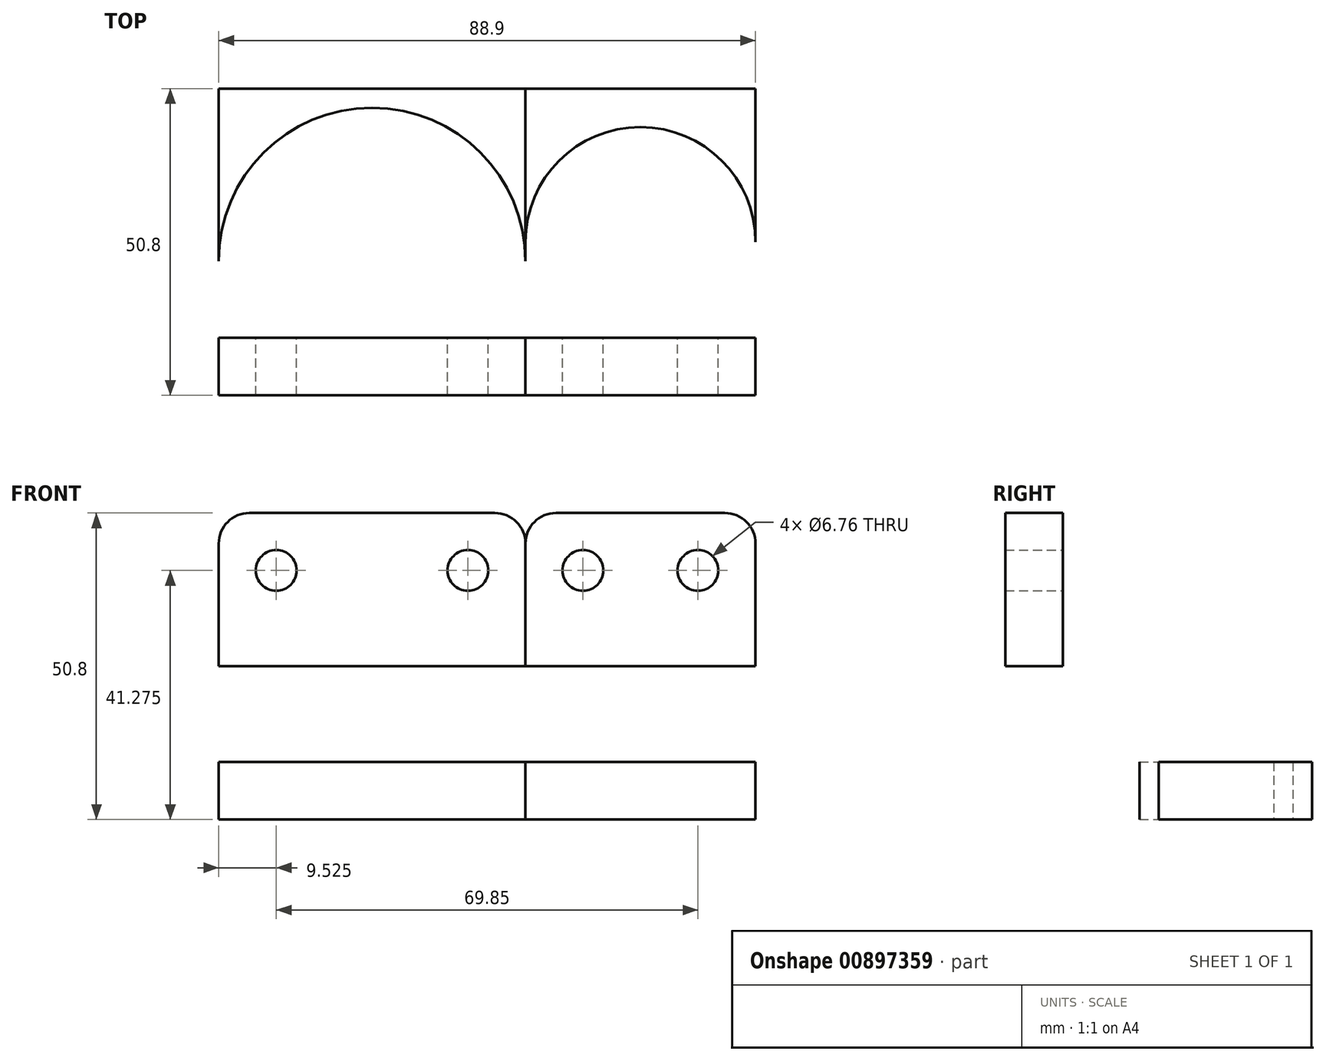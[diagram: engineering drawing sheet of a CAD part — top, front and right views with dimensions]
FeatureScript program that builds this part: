
annotation { "Feature Type Name" : "Feature", "Feature Type Description" : "" }
export const myFeature = defineFeature(function(context is Context, id is Id, definition is map)
    precondition{}
    {
        {
            var Q0;
            Q0=qCreatedBy(makeId("Right.planeOp"),FACE);
            var sketch = newSketch(context, id + "F0", { "sketchPlane" : qUnion([Q0])});
            skLineSegment(sketch, "E0", {"start": v(0, 50.8) * mm, "end": v(0, 0) * mm});
            skLineSegment(sketch, "E1", {"start": v(0, 0) * mm, "end": v(50.8, 0) * mm});
            skLineSegment(sketch, "E2.0", {"start": v(9.53, 9.53) * mm, "end": v(50.8, 9.53) * mm});
            skLineSegment(sketch, "E2.1", {"start": v(9.53, 50.8) * mm, "end": v(9.53, 9.53) * mm});
            skLineSegment(sketch, "E3", {"start": v(0, 50.8) * mm, "end": v(9.53, 50.8) * mm});
            skLineSegment(sketch, "E4", {"start": v(50.8, 9.53) * mm, "end": v(50.8, 0) * mm});
            skSolve(sketch);
        }
        {
            var Q0;
            Q0=makeQuery(id+"F0.imprint","IMPRINT",FACE,{"disambiguationData":[TD([[makeQuery(id+"F0.imprint","IMPRINT",EDGE,{"derivedFrom":sQuery(id+"F0.wireOp",EDGE,"E0")}),1.0]])]});
            extrude(context, id + "F1", {"entities" : qUnion([Q0]), "depth" : 38.1 * mm, "offsetDistance" : 25.4 * mm});
        }
        {
            var Q0;
            Q0 = qSketchRegion(id + "F0", true);
            extrude(context, id + "F2", {"entities" : qUnion([Q0]), "oppositeDirection" : true, "depth" : 50.8 * mm, "offsetDistance" : 25.4 * mm});
        }
        {
            var Q0;
            Q0=makeQuery(id+"F1.opExtrude","SWEPT_FACE",FACE,{"disambiguationData":[OSD([sQuery(id+"F0.wireOp",EDGE,"E1")])]});
            var sketch = newSketch(context, id + "F3", { "sketchPlane" : qUnion([Q0])});
            skCircle(sketch, "E5", {"center": v(19.05, -22.23) * mm, "radius": 6.35 * mm});
            skPoint(sketch, "E6", {"position": v(19.05, -25.4) * mm});
            skArc(sketch, "E7", {"start": v(38.1, -25.4) * mm, "mid": v(19.05, -44.45) * mm, "end": v(0, -25.4) * mm});
            skPoint(sketch, "E8", {"position": v(19.05, -44.45) * mm});
            skLineSegment(sketch, "E9", {"start": v(38.1, -9.52) * mm, "end": v(0, -9.53) * mm, "construction": true});
            skSolve(sketch);
        }
        {
            var Q0;
            Q0=makeQuery(id+"F2.opExtrude","SWEPT_FACE",FACE,{"disambiguationData":[OSD([sQuery(id+"F0.wireOp",EDGE,"E1")])]});
            var sketch = newSketch(context, id + "F4", { "sketchPlane" : qUnion([Q0])});
            skCircle(sketch, "E10", {"center": v(-25.4, -19.05) * mm, "radius": 6.35 * mm});
            skPoint(sketch, "E11", {"position": v(-25.4, -22.23) * mm});
            skArc(sketch, "E12", {"start": v(0, -22.23) * mm, "mid": v(-25.4, -47.62) * mm, "end": v(-50.8, -22.22) * mm});
            skPoint(sketch, "E13", {"position": v(-25.4, -47.62) * mm});
            skSolve(sketch);
        }
        {
            var Q0;
            Q0=makeQuery(id+"F3.imprint","IMPRINT",FACE,{"disambiguationData":[TD([[makeQuery(id+"F3.imprint","IMPRINT",EDGE,{"derivedFrom":sQuery(id+"F3.wireOp",EDGE,"E5")}),1.0]])]});
            var Q1;
            {var subQ0=sQuery(id+"F3.wireOp",EDGE,"E7");Q1=makeQuery(id+"F3.imprint","IMPRINT",FACE,{"disambiguationData":[TD([[makeQuery(id+"F3.imprint","IMPRINT",EDGE,{"derivedFrom":subQ0}),1.0]])]});}
            var Q2;
            Q2=makeQuery(id+"F4.imprint","IMPRINT",FACE,{"disambiguationData":[TD([[makeQuery(id+"F4.imprint","IMPRINT",EDGE,{"derivedFrom":sQuery(id+"F4.wireOp",EDGE,"E10")}),1.0]])]});
            var Q3;
            {var subQ0=sQuery(id+"F4.wireOp",EDGE,"E12");Q3=makeQuery(id+"F4.imprint","IMPRINT",FACE,{"disambiguationData":[TD([[makeQuery(id+"F4.imprint","IMPRINT",EDGE,{"derivedFrom":subQ0}),1.0]])]});}
            extrude(context, id + "F5", {"entities" : qUnion([Q0, Q1, Q2, Q3]), "operationType" : NewBodyOperationType.REMOVE, "oppositeDirection" : true, "depth" : 25.4 * mm, "offsetDistance" : 25.4 * mm});
        }
        {
            var Q0;
            Q0=makeQuery(id+"F1.opExtrude","SWEPT_FACE",FACE,{"disambiguationData":[OSD([sQuery(id+"F0.wireOp",EDGE,"E2.1")])]});
            var sketch = newSketch(context, id + "F6", { "sketchPlane" : qUnion([Q0])});
            skLineSegment(sketch, "E14.bottom", {"start": v(-28.58, 41.28) * mm, "end": v(-9.53, 41.28) * mm, "construction": true});
            skLineSegment(sketch, "E14.top", {"start": v(-28.57, 15.88) * mm, "end": v(-9.52, 15.88) * mm, "construction": true});
            skLineSegment(sketch, "E14.left", {"start": v(-28.58, 41.28) * mm, "end": v(-28.57, 15.88) * mm, "construction": true});
            skLineSegment(sketch, "E14.right", {"start": v(-9.53, 41.28) * mm, "end": v(-9.52, 15.88) * mm, "construction": true});
            skLineSegment(sketch, "E15", {"start": v(-44.84, 0) * mm, "end": v(6.91, 0) * mm, "construction": true});
            skLineSegment(sketch, "E16.bottom", {"start": v(9.53, 41.28) * mm, "end": v(41.28, 41.28) * mm, "construction": true});
            skLineSegment(sketch, "E16.top", {"start": v(9.52, 15.88) * mm, "end": v(41.28, 15.88) * mm, "construction": true});
            skLineSegment(sketch, "E16.left", {"start": v(9.53, 41.28) * mm, "end": v(9.53, 15.88) * mm, "construction": true});
            skLineSegment(sketch, "E16.right", {"start": v(41.28, 41.28) * mm, "end": v(41.28, 15.88) * mm, "construction": true});
            skSolve(sketch);
        }
        {
            var Q0;
            Q0=sQuery(id+"F6.wireOp",VERTEX,"E14.bottom.start");
            var Q1;
            Q1=sQuery(id+"F6.wireOp",VERTEX,"E14.bottom.end");
            var Q2;
            Q2=sQuery(id+"F6.wireOp",VERTEX,"E14.top.end");
            var Q3;
            Q3=sQuery(id+"F6.wireOp",VERTEX,"E14.top.start");
            var Q4;
            Q4=sQuery(id+"F6.wireOp",VERTEX,"E16.bottom.start");
            var Q5;
            Q5=sQuery(id+"F6.wireOp",VERTEX,"E16.top.start");
            var Q6;
            Q6=sQuery(id+"F6.wireOp",VERTEX,"E16.top.end");
            var Q7;
            Q7=sQuery(id+"F6.wireOp",VERTEX,"E16.bottom.end");
            var Q8;
            Q8=makeQuery(id+"F1.opExtrude","SWEPT_BODY",BODY,{"disambiguationData":[OSD([sQuery(id+"F0.wireOp",EDGE,"E0"),sQuery(id+"F0.wireOp",EDGE,"E1"),sQuery(id+"F0.wireOp",EDGE,"E2.0"),sQuery(id+"F0.wireOp",EDGE,"E2.1"),sQuery(id+"F0.wireOp",EDGE,"E3"),sQuery(id+"F0.wireOp",EDGE,"E4")])]});
            var Q9;
            Q9=makeQuery(id+"F2.opExtrude","SWEPT_BODY",BODY,{"disambiguationData":[OSD([sQuery(id+"F0.wireOp",EDGE,"E0"),sQuery(id+"F0.wireOp",EDGE,"E1"),sQuery(id+"F0.wireOp",EDGE,"E2.0"),sQuery(id+"F0.wireOp",EDGE,"E2.1"),sQuery(id+"F0.wireOp",EDGE,"E3"),sQuery(id+"F0.wireOp",EDGE,"E4")])]});
            hole(context, id + "F7", {"style" : HoleStyle.SIMPLE, "endStyle" : HoleEndStyle.THROUGH, "standardTappedOrClearance" : lookupTablePath({ "fit" : "Free", "standard" : "ANSI", "size" : "1/4", "type" : "Clearance" }), "standardBlindInLast" : lookupTablePath({ "fit" : "Free", "standard" : "ANSI", "engagement" : "75%", "pitch" : "20 tpi", "size" : "1/4", "type" : "Clearance & tapped" }), "holeDiameter" : 6.76 * mm, "majorDiameter" : 6.35 * mm, "isTappedThrough" : true, "tappedDepth" : 12.7 * mm, "tapClearance" : 3, "locations" : qUnion([Q0, Q1, Q2, Q3, Q4, Q5, Q6, Q7]), "scope" : qUnion([Q8, Q9])});
        }
        {
            var Q0;
            Q0=makeQuery(id+"F1.opExtrude","CAP_EDGE",EDGE,{"disambiguationData":[OSD([sQuery(id+"F0.wireOp",EDGE,"E3")])],"isStart":false});
            var Q1;
            Q1=makeQuery(id+"F1.opExtrude","CAP_EDGE",EDGE,{"disambiguationData":[OSD([sQuery(id+"F0.wireOp",EDGE,"E3")])],"isStart":true});
            var Q2;
            Q2=makeQuery(id+"F2.opExtrude","CAP_EDGE",EDGE,{"disambiguationData":[OSD([sQuery(id+"F0.wireOp",EDGE,"E3")])],"isStart":false});
            var Q3;
            Q3=makeQuery(id+"F2.opExtrude","CAP_EDGE",EDGE,{"disambiguationData":[OSD([sQuery(id+"F0.wireOp",EDGE,"E3")])],"isStart":true});
            fillet(context, id + "F8", {"entities" : qUnion([Q0, Q1, Q2, Q3]), "tangentPropagation" : true, "radius" : 5.08 * mm, "defaultsChanged" : false, "vertexSettings" : [], "allowEdgeOverflow" : false});
        }
    });
